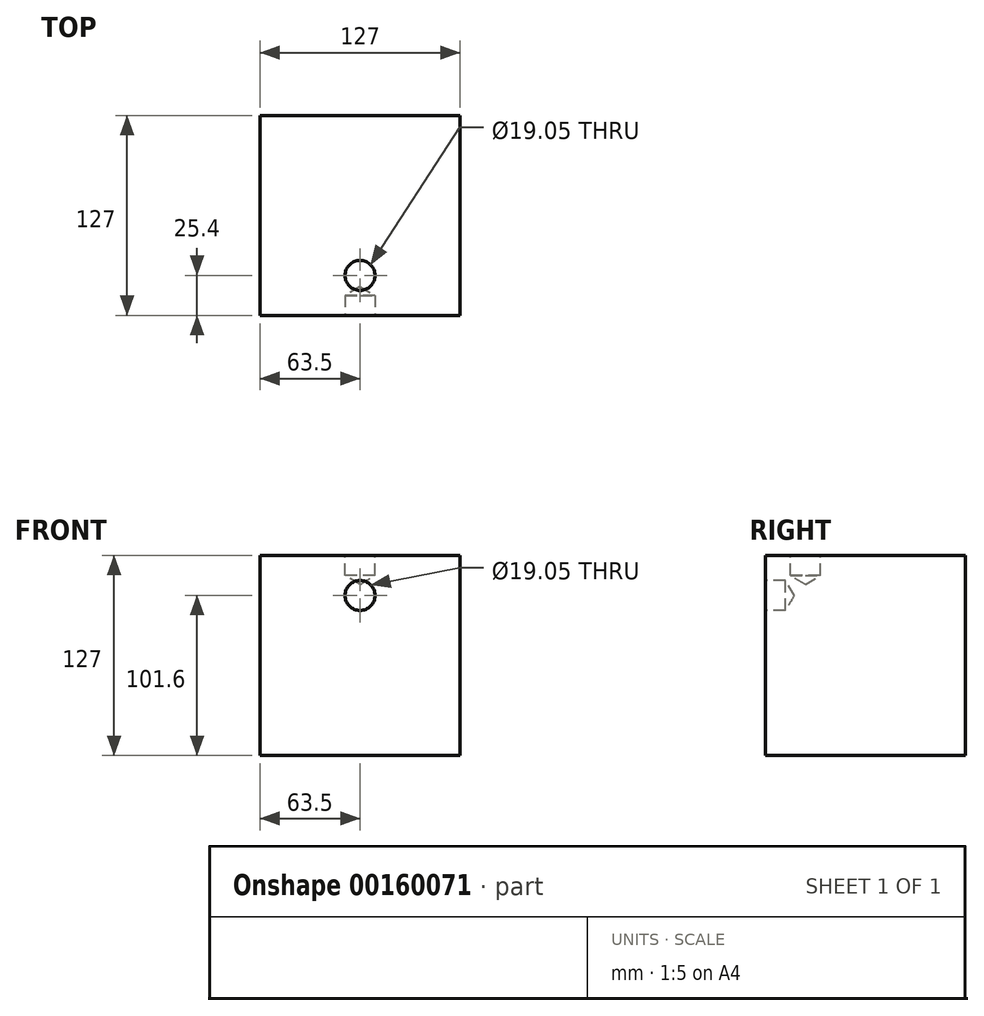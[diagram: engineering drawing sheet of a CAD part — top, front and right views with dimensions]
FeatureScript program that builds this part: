
annotation { "Feature Type Name" : "Feature", "Feature Type Description" : "" }
export const myFeature = defineFeature(function(context is Context, id is Id, definition is map)
    precondition{}
    {
        {
            var Q0;
            Q0=qCreatedBy(makeId("Front.planeOp"),FACE);
            var sketch = newSketch(context, id + "F0", { "sketchPlane" : qUnion([Q0])});
            skLineSegment(sketch, "E0.bottom", {"start": v(0, 0) * mm, "end": v(-127, 0) * mm});
            skLineSegment(sketch, "E0.top", {"start": v(0, 127) * mm, "end": v(-127, 127) * mm});
            skLineSegment(sketch, "E0.left", {"start": v(0, 0) * mm, "end": v(0, 127) * mm});
            skLineSegment(sketch, "E0.right", {"start": v(-127, 0) * mm, "end": v(-127, 127) * mm});
            skSolve(sketch);
        }
        {
            var Q0;
            Q0=makeQuery(id+"F0.imprint","IMPRINT",FACE,{"disambiguationData":[TD([[makeQuery(id+"F0.imprint","IMPRINT",EDGE,{"derivedFrom":sQuery(id+"F0.wireOp",EDGE,"E0.bottom")}),-1.0]])]});
            extrude(context, id + "F1", {"entities" : qUnion([Q0]), "depth" : 127 * mm});
        }
        {
            var Q0;
            Q0=makeQuery(id+"F1.opExtrude","CAP_FACE",FACE,{"disambiguationData":[OSD([sQuery(id+"F0.wireOp",EDGE,"E0.bottom"),sQuery(id+"F0.wireOp",EDGE,"E0.top"),sQuery(id+"F0.wireOp",EDGE,"E0.left"),sQuery(id+"F0.wireOp",EDGE,"E0.right")])],"isStart":false});
            var sketch = newSketch(context, id + "F2", { "sketchPlane" : qUnion([Q0])});
            skLineSegment(sketch, "E1.bottom", {"start": v(-127, 127) * mm, "end": v(0, 127) * mm});
            skLineSegment(sketch, "E1.top", {"start": v(-127, 76.2) * mm, "end": v(0, 76.2) * mm});
            skLineSegment(sketch, "E1.left", {"start": v(-127, 127) * mm, "end": v(-127, 76.2) * mm});
            skLineSegment(sketch, "E1.right", {"start": v(0, 127) * mm, "end": v(0, 76.2) * mm});
            skCircle(sketch, "E2", {"center": v(-63.5, 101.6) * mm, "radius": 9.53 * mm});
            skPoint(sketch, "E2.centerSnap0", {"position": v(-63.5, 76.2) * mm});
            skPoint(sketch, "E2.centerSnap1", {"position": v(-127, 101.6) * mm});
            skSolve(sketch);
        }
        {
            var Q0;
            Q0=sQuery(id+"F2.wireOp",VERTEX,"E2.center");
            var Q1;
            Q1=makeQuery(id+"F1.opExtrude","SWEPT_BODY",BODY,{"disambiguationData":[OSD([sQuery(id+"F0.wireOp",EDGE,"E0.bottom"),sQuery(id+"F0.wireOp",EDGE,"E0.top"),sQuery(id+"F0.wireOp",EDGE,"E0.left"),sQuery(id+"F0.wireOp",EDGE,"E0.right")])]});
            hole(context, id + "F3", {"style" : HoleStyle.SIMPLE, "endStyle" : HoleEndStyle.BLIND, "holeDiameter" : 19.05 * mm, "holeDepth" : 12.7 * mm, "locations" : qUnion([Q0]), "scope" : qUnion([Q1])});
        }
        {
            var Q0;
            Q0=makeQuery(id+"F1.opExtrude","SWEPT_FACE",FACE,{"disambiguationData":[OSD([sQuery(id+"F0.wireOp",EDGE,"E0.top")])]});
            var sketch = newSketch(context, id + "F4", { "sketchPlane" : qUnion([Q0])});
            skLineSegment(sketch, "E3.bottom", {"start": v(-127, -127) * mm, "end": v(0, -127) * mm});
            skLineSegment(sketch, "E3.top", {"start": v(-127, -76.2) * mm, "end": v(0, -76.2) * mm});
            skLineSegment(sketch, "E3.left", {"start": v(-127, -127) * mm, "end": v(-127, -76.2) * mm});
            skLineSegment(sketch, "E3.right", {"start": v(0, -127) * mm, "end": v(0, -76.2) * mm});
            skPoint(sketch, "E4", {"position": v(-63.5, -101.6) * mm});
            skPoint(sketch, "E4.positionSnap0", {"position": v(0, -101.6) * mm});
            skPoint(sketch, "E4.positionSnap1", {"position": v(-63.5, -76.2) * mm});
            skSolve(sketch);
        }
        {
            var Q0;
            Q0=sQuery(id+"F4.wireOp",VERTEX,"E4");
            var Q1;
            Q1=makeQuery(id+"F1.opExtrude","SWEPT_BODY",BODY,{"disambiguationData":[OSD([sQuery(id+"F0.wireOp",EDGE,"E0.bottom"),sQuery(id+"F0.wireOp",EDGE,"E0.top"),sQuery(id+"F0.wireOp",EDGE,"E0.left"),sQuery(id+"F0.wireOp",EDGE,"E0.right")])]});
            hole(context, id + "F5", {"style" : HoleStyle.SIMPLE, "endStyle" : HoleEndStyle.BLIND, "holeDiameter" : 19.05 * mm, "holeDepth" : 12.7 * mm, "locations" : qUnion([Q0]), "scope" : qUnion([Q1])});
        }
    });
